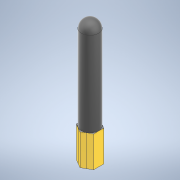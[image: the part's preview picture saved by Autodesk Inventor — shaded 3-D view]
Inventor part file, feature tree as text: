
AUTODESK INVENTOR PART (.ipt)
format: ipt  version: 2020 (Build 240168000, 168)  size: 143,360 bytes
history: native  units: mm
features: other x2, extrude x2, plane x2, sketch x2, fillet x1, projected_geometry x1
ambient origin geometry x8: Origin, YZ Plane, XZ Plane, XY Plane, X Axis, Y Axis, Z Axis, Center Point
bodies: Body1 (feature_tree)
feature tree (10):
  other  "Sólido1"
  extrude  "Extrusión1"  Depth=4.5mm TaperAngle=0.0deg
  fillet  "Empalme1"  Radius=4.5mm
  extrude  "Extrusión2"  Depth=5.196mm
  plane  "Plano de trabajo1"
  plane  "Plano de trabajo2"
  other  "antena"
  sketch  "Boceto1"  dims[d0=9.0mm d1=64.47mm d2=0.0mm d3=4.5mm]
  sketch  "Boceto2"  dims[d9=30.0deg d11=5.196mm d12=5.196mm d13=5.196mm d14=5.196mm d15=16.1175mm d16=0.0mm]
  projected_geometry  "Contorno proyectado1"
